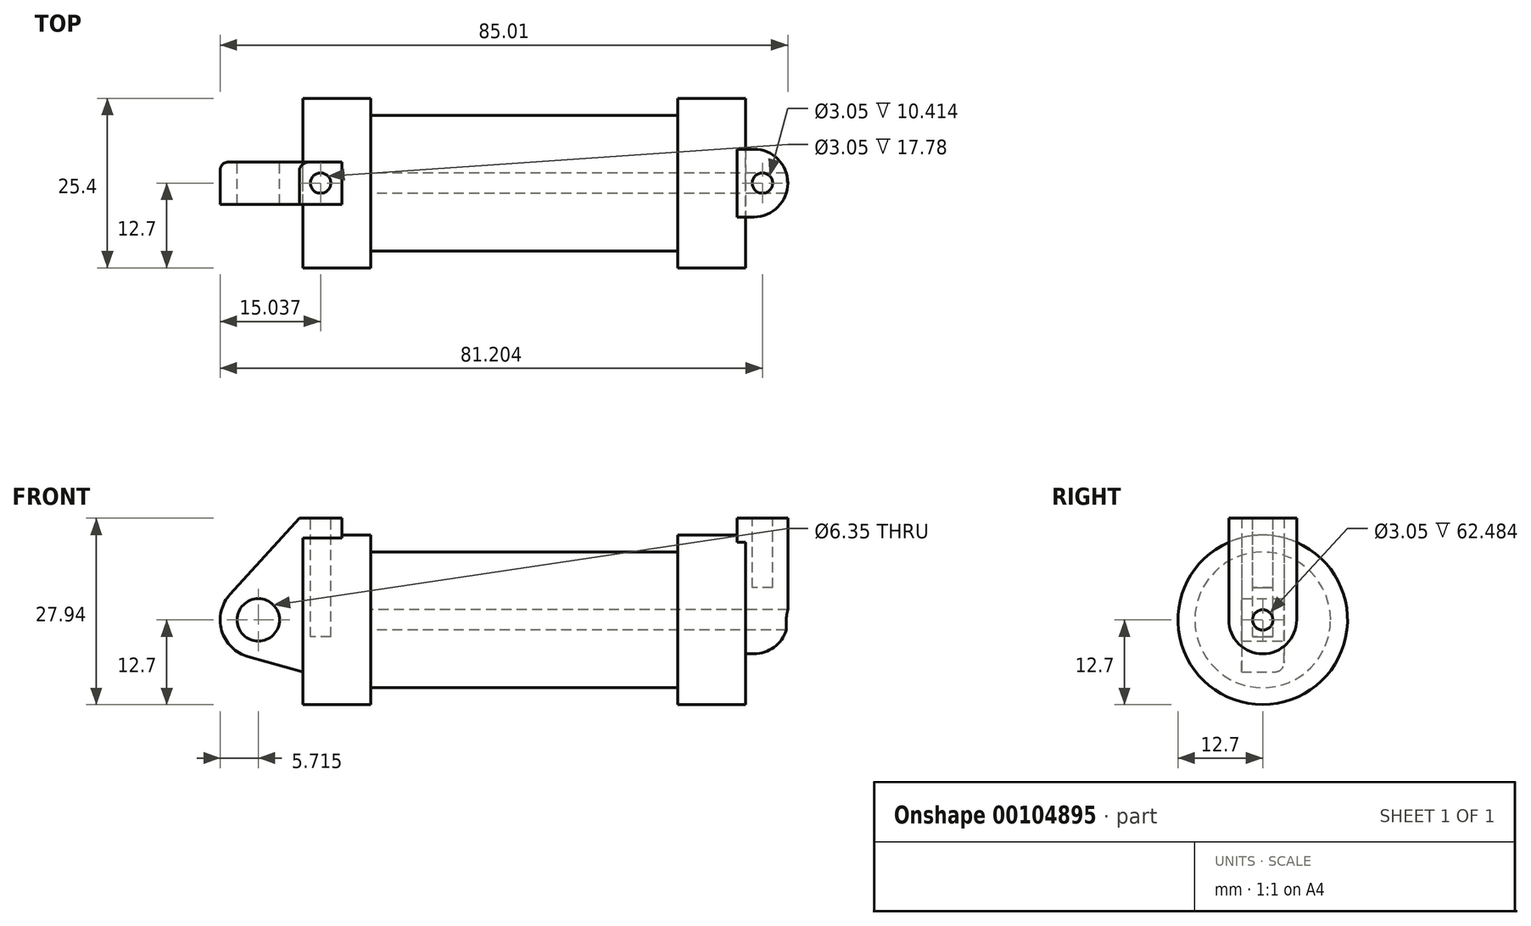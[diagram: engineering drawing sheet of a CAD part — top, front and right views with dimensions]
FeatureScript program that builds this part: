
annotation { "Feature Type Name" : "Feature", "Feature Type Description" : "" }
export const myFeature = defineFeature(function(context is Context, id is Id, definition is map)
    precondition{}
    {
        {
            var Q0;
            Q0=qCreatedBy(makeId("Front.planeOp"),FACE);
            var sketch = newSketch(context, id + "F0", { "sketchPlane" : qUnion([Q0])});
            skLineSegment(sketch, "E0", {"start": v(0, 0) * mm, "end": v(0, 12.7) * mm});
            skLineSegment(sketch, "E1", {"start": v(0, 12.7) * mm, "end": v(10.16, 12.7) * mm});
            skLineSegment(sketch, "E2", {"start": v(10.16, 12.7) * mm, "end": v(10.16, 10.16) * mm});
            skLineSegment(sketch, "E3", {"start": v(10.16, 10.16) * mm, "end": v(56.13, 10.16) * mm});
            skLineSegment(sketch, "E4", {"start": v(56.13, 10.16) * mm, "end": v(56.13, 12.7) * mm});
            skLineSegment(sketch, "E5", {"start": v(56.13, 12.7) * mm, "end": v(66.3, 12.7) * mm});
            skLineSegment(sketch, "E6", {"start": v(66.3, 12.7) * mm, "end": v(66.3, 0) * mm});
            skLineSegment(sketch, "E7", {"start": v(66.3, 0) * mm, "end": v(0, 0) * mm});
            skLineSegment(sketch, "E8", {"start": v(5.84, 15.24) * mm, "end": v(-0.5, 15.24) * mm});
            skLineSegment(sketch, "E9", {"start": v(-0.5, 15.24) * mm, "end": v(-10.88, 3.85) * mm});
            skLineSegment(sketch, "E10", {"start": v(0, 0) * mm, "end": v(-6.65, 0) * mm});
            skCircle(sketch, "E11", {"center": v(-6.65, 0) * mm, "radius": 5.72 * mm});
            skCircle(sketch, "E12", {"center": v(-6.65, 0) * mm, "radius": 3.18 * mm});
            skLineSegment(sketch, "E13", {"start": v(5.84, 15.24) * mm, "end": v(5.84, -9.4) * mm});
            skLineSegment(sketch, "E14", {"start": v(5.84, -9.4) * mm, "end": v(-8.18, -5.5) * mm});
            skSolve(sketch);
        }
        {
            var Q0;
            {var subQ0=sQuery(id+"F0.wireOp",EDGE,"E2");Q0=makeQuery(id+"F0.imprint","IMPRINT",FACE,{"disambiguationData":[TD([[makeQuery(id+"F0.imprint","IMPRINT",EDGE,{"derivedFrom":subQ0}),-1.0]])]});}
            var Q1;
            {var subQ0=sQuery(id+"F0.wireOp",EDGE,"E0");Q1=makeQuery(id+"F0.imprint","IMPRINT",FACE,{"disambiguationData":[TD([[makeQuery(id+"F0.imprint","IMPRINT",EDGE,{"derivedFrom":subQ0}),-1.0]])]});}
            var Q2;
            Q2=sQuery(id+"F0.wireOp",EDGE,"E7");
            revolve(context, id + "F1", {"entities" : qUnion([Q0, Q1]), "axis" : qUnion([Q2]), "revolveType" : RevolveType.FULL});
        }
        {
            var Q0;
            {var subQ3=sQuery(id+"F0.wireOp",EDGE,"E0");Q0=makeQuery(id+"F0.imprint","IMPRINT",FACE,{"disambiguationData":[TD([[makeQuery(id+"F0.imprint","IMPRINT",EDGE,{"derivedFrom":subQ3}),1.0]])]});}
            var Q1;
            {var subQ0=sQuery(id+"F0.wireOp",EDGE,"E0");Q1=makeQuery(id+"F0.imprint","IMPRINT",FACE,{"disambiguationData":[TD([[makeQuery(id+"F0.imprint","IMPRINT",EDGE,{"derivedFrom":subQ0}),-1.0]])]});}
            var Q2;
            {var subQ0=sQuery(id+"F0.wireOp",EDGE,"E14");Q2=makeQuery(id+"F0.imprint","IMPRINT",FACE,{"disambiguationData":[TD([[makeQuery(id+"F0.imprint","IMPRINT",EDGE,{"derivedFrom":subQ0}),-1.0]])]});}
            var Q3;
            {var subQ4=sQuery(id+"F0.wireOp",EDGE,"E12");Q3=makeQuery(id+"F0.imprint","IMPRINT",FACE,{"disambiguationData":[TD([[makeQuery(id+"F0.imprint","IMPRINT",EDGE,{"derivedFrom":subQ4}),-1.0]])]});}
            extrude(context, id + "F2", {"entities" : qUnion([Q0, Q1, Q2, Q3]), "operationType" : NewBodyOperationType.ADD, "endBound" : BoundingType.SYMMETRIC, "depth" : 6.35 * mm});
        }
        {
            var Q0;
            Q0=makeQuery(id+"F1.opRevolve","SWEPT_FACE",FACE,{"disambiguationData":[OSD([sQuery(id+"F0.wireOp",EDGE,"E6")])]});
            var sketch = newSketch(context, id + "F3", { "sketchPlane" : qUnion([Q0])});
            skCircle(sketch, "E15", {"center": v(0, 0) * mm, "radius": 1.52 * mm});
            skCircle(sketch, "E16", {"center": v(0, 0) * mm, "radius": 5.08 * mm});
            skLineSegment(sketch, "E17", {"start": v(5.08, 0) * mm, "end": v(5.08, 15.24) * mm});
            skLineSegment(sketch, "E18", {"start": v(5.08, 15.24) * mm, "end": v(-5.08, 15.24) * mm});
            skLineSegment(sketch, "E19", {"start": v(-5.08, 15.24) * mm, "end": v(-5.08, 0) * mm});
            skSolve(sketch);
        }
        {
            var Q0;
            Q0 = qSketchRegion(id + "F3", true);
            extrude(context, id + "F4", {"entities" : qUnion([Q0]), "operationType" : NewBodyOperationType.ADD, "depth" : 6.35 * mm, "hasSecondDirection" : true, "secondDirectionOppositeDirection" : true, "secondDirectionDepth" : 1.27 * mm});
        }
        {
            var Q0;
            Q0=makeQuery(id+"F4.opExtrude","SWEPT_FACE",FACE,{"disambiguationData":[OSD([sQuery(id+"F3.wireOp",EDGE,"E18")])]});
            var sketch = newSketch(context, id + "F5", { "sketchPlane" : qUnion([Q0])});
            skCircle(sketch, "E20", {"center": v(68.83, 0) * mm, "radius": 1.52 * mm});
            skPoint(sketch, "E21", {"position": v(65.02, 0) * mm});
            skPoint(sketch, "E22", {"position": v(68.83, 5.08) * mm});
            skSolve(sketch);
        }
        {
            var Q0;
            Q0 = qSketchRegion(id + "F5", true);
            var Q1;
            Q1=sQuery(id+"F5.wireOp",EDGE,"E20");
            extrude(context, id + "F6", {"entities" : qUnion([Q0]), "operationType" : NewBodyOperationType.REMOVE, "surfaceEntities" : qUnion([Q1]), "oppositeDirection" : true, "depth" : 10.4 * mm});
        }
        {
            var Q0;
            Q0=makeQuery(id+"F2.opExtrude","SWEPT_FACE",FACE,{"disambiguationData":[OSD([sQuery(id+"F0.wireOp",EDGE,"E8")])]});
            var sketch = newSketch(context, id + "F7", { "sketchPlane" : qUnion([Q0])});
            skCircle(sketch, "E23", {"center": v(2.67, 0) * mm, "radius": 1.52 * mm});
            skSolve(sketch);
        }
        {
            var Q0;
            Q0=makeQuery(id+"F7.imprint","IMPRINT",FACE,{"disambiguationData":[TD([[makeQuery(id+"F7.imprint","IMPRINT",EDGE,{"derivedFrom":sQuery(id+"F7.wireOp",EDGE,"E23")}),1.0]])]});
            var Q1;
            Q1=sQuery(id+"F7.wireOp",EDGE,"E23");
            extrude(context, id + "F8", {"entities" : qUnion([Q0]), "operationType" : NewBodyOperationType.REMOVE, "surfaceEntities" : qUnion([Q1]), "oppositeDirection" : true, "depth" : 17.78 * mm});
        }
        {
            var Q0;
            Q0=makeQuery(id+"F4.boolean.opBoolean","SPLIT",FACE,{"disambiguationData":[TD([makeQuery(id+"F4.opExtrude","SWEPT_FACE",FACE,{"disambiguationData":[OSD([sQuery(id+"F3.wireOp",EDGE,"E15")])]})])],"derivedFrom":makeQuery(id+"F1.opRevolve","SWEPT_FACE",FACE,{"disambiguationData":[OSD([sQuery(id+"F0.wireOp",EDGE,"E6")])]})});
            var Q1;
            Q1=makeQuery(id+"F1.opRevolve","SWEPT_FACE",FACE,{"disambiguationData":[OSD([sQuery(id+"F0.wireOp",EDGE,"E2")])]});
            extrude(context, id + "F9", {"entities" : qUnion([Q0]), "operationType" : NewBodyOperationType.REMOVE, "endBound" : BoundingType.UP_TO_SURFACE, "oppositeDirection" : true, "endBoundEntityFace" : qUnion([Q1]), "depth" : 25.4 * mm});
        }
        {
            var Q0;
            Q0=makeQuery(id+"F2.opExtrude","CAP_EDGE",EDGE,{"disambiguationData":[OSD([sQuery(id+"F0.wireOp",EDGE,"E11")])],"isStart":true});
            var Q1;
            Q1=makeQuery(id+"F2.opExtrude","CAP_EDGE",EDGE,{"disambiguationData":[OSD([sQuery(id+"F0.wireOp",EDGE,"E9")])],"isStart":true});
            fillet(context, id + "F10", {"entities" : qUnion([Q0, Q1]), "radius" : 1.27 * mm, "tangentPropagation" : true, "allowEdgeOverflow" : false});
        }
        {
            var Q0;
            Q0=makeQuery(id+"F4.opExtrude","CAP_EDGE",EDGE,{"disambiguationData":[OSD([sQuery(id+"F3.wireOp",EDGE,"E19")])],"isStart":false});
            var Q1;
            Q1=makeQuery(id+"F4.opExtrude","CAP_EDGE",EDGE,{"disambiguationData":[OSD([sQuery(id+"F3.wireOp",EDGE,"E16")])],"isStart":false});
            fillet(context, id + "F11", {"entities" : qUnion([Q0, Q1]), "radius" : 5.08 * mm, "tangentPropagation" : true, "allowEdgeOverflow" : false});
        }
    });
